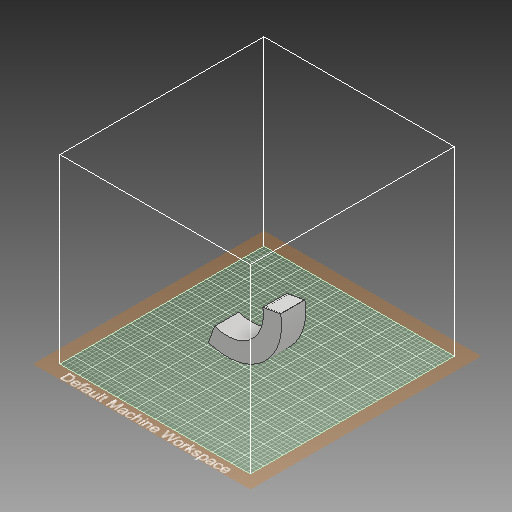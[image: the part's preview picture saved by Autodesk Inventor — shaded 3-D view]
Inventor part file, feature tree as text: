
AUTODESK INVENTOR PART (.ipt)
format: ipt  version: 2019 (Build 230136000, 136)  size: 343,552 bytes
history: native  units: mm
features: extrude x3, sketch x2, pattern_circular x1, other x1, mirror x1
ambient origin geometry x8: Origin, YZ Plane, XZ Plane, XY Plane, X Axis, Y Axis, Z Axis, Center Point
bodies: Solide1 (feature_tree)
feature tree (8):
  sketch  "Esquisse1"
  extrude  "Extrusion2"  Depth=200.0mm
  extrude  "Extrusion3"  Depth=1.745329mm
  pattern_circular  "Réseau circulaire1"  [2 undecoded]
  extrude  "Extrusion4"  Depth=40.0mm
  other  "Plan de construction1"
  mirror  "Symétrie1"
  sketch  "Esquisse2"
note: 2 required parameter values undecoded (feature->parameter linkage not recoverable at this tier; creation-order binding heuristic only, values carry confidence <= 0.55)
